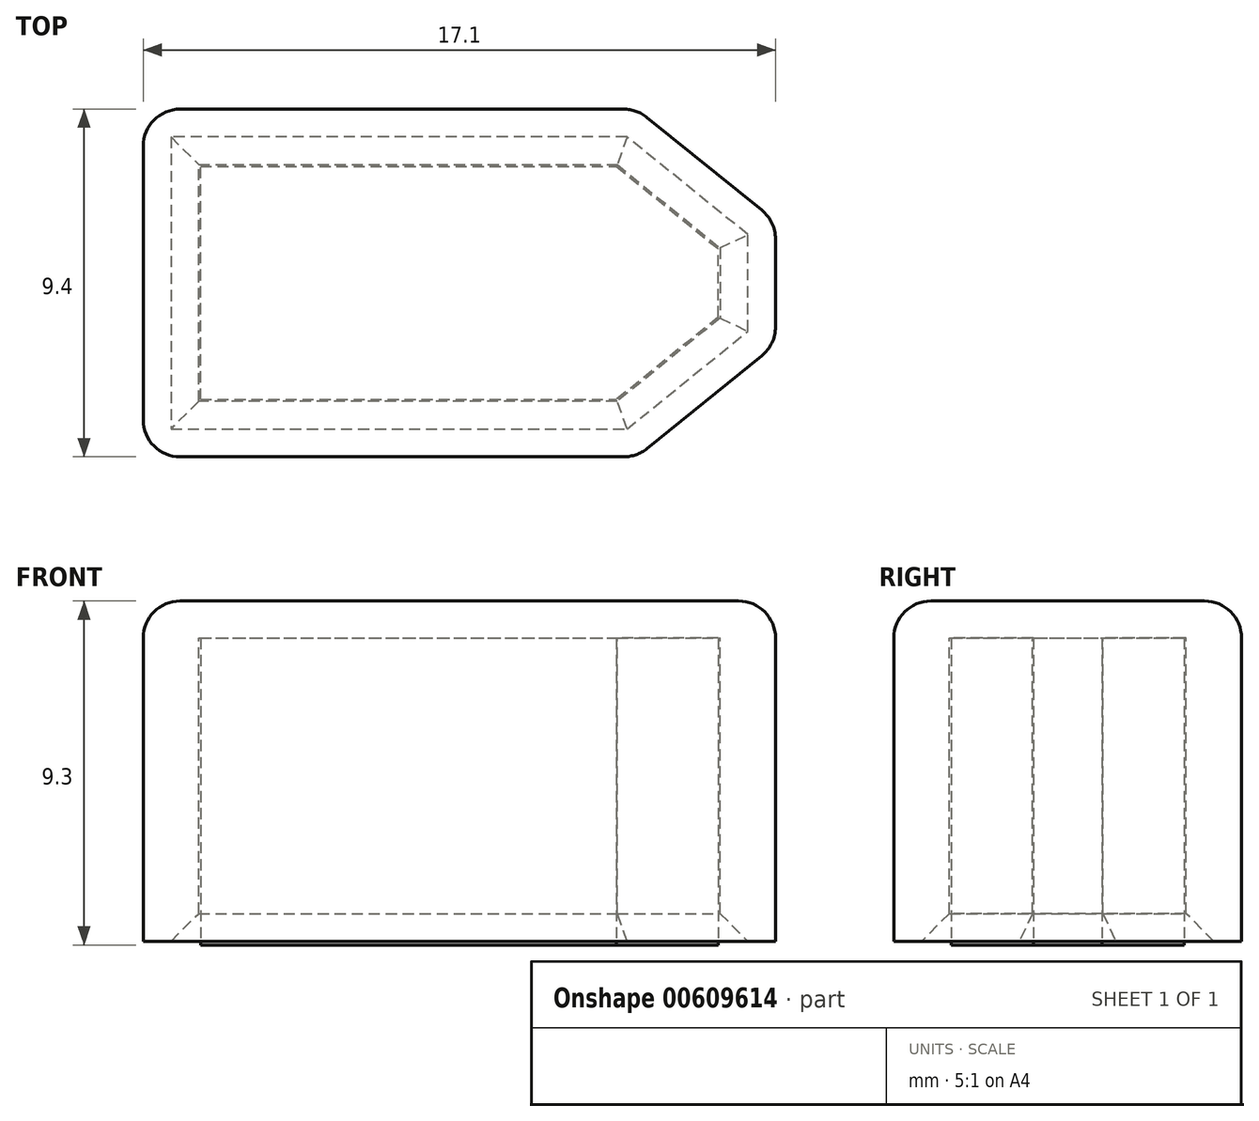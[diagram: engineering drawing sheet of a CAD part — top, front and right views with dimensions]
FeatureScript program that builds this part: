
annotation { "Feature Type Name" : "Feature", "Feature Type Description" : "" }
export const myFeature = defineFeature(function(context is Context, id is Id, definition is map)
    precondition{}
    {
        {
            var Q0;
            Q0=qCreatedBy(makeId("Top.planeOp"),FACE);
            var sketch = newSketch(context, id + "F0", { "sketchPlane" : qUnion([Q0])});
            skLineSegment(sketch, "E0.bottom", {"start": v(0, 0) * mm, "end": v(11.25, 0) * mm});
            skLineSegment(sketch, "E0.top", {"start": v(0, 6.3) * mm, "end": v(11.25, 6.3) * mm});
            skLineSegment(sketch, "E0.left", {"start": v(0, 0) * mm, "end": v(0, 6.3) * mm});
            skLineSegment(sketch, "E0.right", {"start": v(14, 2.22) * mm, "end": v(14, 4.08) * mm});
            skLineSegment(sketch, "E1", {"start": v(11.25, 6.3) * mm, "end": v(14, 4.08) * mm});
            skLineSegment(sketch, "E2", {"start": v(14, 2.22) * mm, "end": v(11.25, 0) * mm});
            skLineSegment(sketch, "E3", {"start": v(11.25, 6.3) * mm, "end": v(11.25, 0) * mm, "construction": true});
            skPoint(sketch, "E4.orphan", {"position": v(14, 0) * mm});
            skSolve(sketch);
        }
        {
            var Q0;
            Q0=makeQuery(id+"F0.imprint","IMPRINT",FACE,{"disambiguationData":[TD([[makeQuery(id+"F0.imprint","IMPRINT",EDGE,{"derivedFrom":sQuery(id+"F0.wireOp",EDGE,"E0.bottom")}),1.0]])]});
            extrude(context, id + "F1", {"entities" : qUnion([Q0]), "depth" : 8.3 * mm, "offsetDistance" : 25 * mm});
        }
        {
            var Q0;
            Q0=makeQuery(id+"F1.opExtrude","CAP_FACE",FACE,{"disambiguationData":[OSD([sQuery(id+"F0.wireOp",EDGE,"E0.bottom"),sQuery(id+"F0.wireOp",EDGE,"E0.top"),sQuery(id+"F0.wireOp",EDGE,"E0.left"),sQuery(id+"F0.wireOp",EDGE,"E0.right"),sQuery(id+"F0.wireOp",EDGE,"E1"),sQuery(id+"F0.wireOp",EDGE,"E2")])],"isStart":false});
            var sketch = newSketch(context, id + "F2", { "sketchPlane" : qUnion([Q0])});
            skLineSegment(sketch, "E5.0", {"start": v(-0.05, -0.05) * mm, "end": v(-0.05, 6.35) * mm});
            skLineSegment(sketch, "E5.1", {"start": v(11.27, 6.35) * mm, "end": v(14.05, 4.1) * mm});
            skLineSegment(sketch, "E5.2", {"start": v(14.05, 2.2) * mm, "end": v(14.05, 4.1) * mm});
            skLineSegment(sketch, "E5.3", {"start": v(-0.05, 6.35) * mm, "end": v(11.27, 6.35) * mm});
            skLineSegment(sketch, "E5.4", {"start": v(14.05, 2.2) * mm, "end": v(11.27, -0.05) * mm});
            skLineSegment(sketch, "E5.5", {"start": v(-0.05, -0.05) * mm, "end": v(11.27, -0.05) * mm});
            skLineSegment(sketch, "E6.0", {"start": v(-1.55, -1.55) * mm, "end": v(-1.55, 7.85) * mm});
            skLineSegment(sketch, "E6.1", {"start": v(11.8, 7.85) * mm, "end": v(15.55, 4.81) * mm});
            skLineSegment(sketch, "E6.2", {"start": v(15.55, 1.49) * mm, "end": v(15.55, 4.81) * mm});
            skLineSegment(sketch, "E6.3", {"start": v(-1.55, 7.85) * mm, "end": v(11.8, 7.85) * mm});
            skLineSegment(sketch, "E6.4", {"start": v(15.55, 1.49) * mm, "end": v(11.8, -1.55) * mm});
            skLineSegment(sketch, "E6.5", {"start": v(-1.55, -1.55) * mm, "end": v(11.8, -1.55) * mm});
            skSolve(sketch);
        }
        {
            var Q0;
            Q0=makeQuery(id+"F2.imprint","IMPRINT",FACE,{"disambiguationData":[TD([[makeQuery(id+"F2.imprint","IMPRINT",EDGE,{"derivedFrom":sQuery(id+"F2.wireOp",EDGE,"E5.0")}),1.0]])]});
            extrude(context, id + "F3", {"entities" : qUnion([Q0]), "oppositeDirection" : true, "depth" : 8.2 * mm, "offsetDistance" : 25 * mm});
        }
        {
            var Q0;
            Q0=makeQuery(id+"F3.opExtrude","CAP_FACE",FACE,{"disambiguationData":[OSD([sQuery(id+"F2.wireOp",EDGE,"E5.0"),sQuery(id+"F2.wireOp",EDGE,"E5.1"),sQuery(id+"F2.wireOp",EDGE,"E5.2"),sQuery(id+"F2.wireOp",EDGE,"E5.3"),sQuery(id+"F2.wireOp",EDGE,"E5.4"),sQuery(id+"F2.wireOp",EDGE,"E5.5"),sQuery(id+"F2.wireOp",EDGE,"E6.0"),sQuery(id+"F2.wireOp",EDGE,"E6.1"),sQuery(id+"F2.wireOp",EDGE,"E6.2"),sQuery(id+"F2.wireOp",EDGE,"E6.3"),sQuery(id+"F2.wireOp",EDGE,"E6.4"),sQuery(id+"F2.wireOp",EDGE,"E6.5")])],"isStart":true});
            var sketch = newSketch(context, id + "F4", { "sketchPlane" : qUnion([Q0])});
            skLineSegment(sketch, "E7", {"start": v(-1.55, 7.85) * mm, "end": v(-1.55, -1.55) * mm});
            skLineSegment(sketch, "E8", {"start": v(-1.55, -1.55) * mm, "end": v(11.8, -1.55) * mm});
            skLineSegment(sketch, "E9", {"start": v(11.8, -1.55) * mm, "end": v(15.55, 1.49) * mm});
            skLineSegment(sketch, "E10", {"start": v(15.55, 1.49) * mm, "end": v(15.55, 4.81) * mm});
            skLineSegment(sketch, "E11", {"start": v(15.55, 4.81) * mm, "end": v(11.8, 7.85) * mm});
            skLineSegment(sketch, "E12", {"start": v(11.8, 7.85) * mm, "end": v(-1.55, 7.85) * mm});
            skSolve(sketch);
        }
        {
            var Q0;
            Q0 = qSketchRegion(id + "F4", true);
            extrude(context, id + "F5", {"entities" : qUnion([Q0]), "operationType" : NewBodyOperationType.ADD, "depth" : 1 * mm, "offsetDistance" : 25 * mm});
        }
        {
            var Q0;
            Q0=makeQuery(id+"F5.opExtrude","CAP_FACE",FACE,{"disambiguationData":[OSD([sQuery(id+"F4.wireOp",EDGE,"E7"),sQuery(id+"F4.wireOp",EDGE,"E8"),sQuery(id+"F4.wireOp",EDGE,"E9"),sQuery(id+"F4.wireOp",EDGE,"E10"),sQuery(id+"F4.wireOp",EDGE,"E11"),sQuery(id+"F4.wireOp",EDGE,"E12")])],"isStart":false});
            var Q1;
            Q1=makeQuery(id+"F5.boolean.opBoolean","MERGE",EDGE,{"derivedFrom":[makeQuery(id+"F3.opExtrude","SWEPT_EDGE",EDGE,{"disambiguationData":[OSD([sQuery(id+"F2.wireOp",EDGE,"E6.0"),sQuery(id+"F2.wireOp",EDGE,"E6.5")])]}),makeQuery(id+"F5.opExtrude","SWEPT_EDGE",EDGE,{"disambiguationData":[OSD([sQuery(id+"F4.wireOp",EDGE,"E7"),sQuery(id+"F4.wireOp",EDGE,"E8")])]})]});
            var Q2;
            Q2=makeQuery(id+"F5.boolean.opBoolean","MERGE",EDGE,{"derivedFrom":[makeQuery(id+"F3.opExtrude","SWEPT_EDGE",EDGE,{"disambiguationData":[OSD([sQuery(id+"F2.wireOp",EDGE,"E6.0"),sQuery(id+"F2.wireOp",EDGE,"E6.3")])]}),makeQuery(id+"F5.opExtrude","SWEPT_EDGE",EDGE,{"disambiguationData":[OSD([sQuery(id+"F4.wireOp",EDGE,"E7"),sQuery(id+"F4.wireOp",EDGE,"E12")])]})]});
            var Q3;
            Q3=makeQuery(id+"F5.boolean.opBoolean","MERGE",EDGE,{"derivedFrom":[makeQuery(id+"F3.opExtrude","SWEPT_EDGE",EDGE,{"disambiguationData":[OSD([sQuery(id+"F2.wireOp",EDGE,"E6.1"),sQuery(id+"F2.wireOp",EDGE,"E6.3")])]}),makeQuery(id+"F5.opExtrude","SWEPT_EDGE",EDGE,{"disambiguationData":[OSD([sQuery(id+"F4.wireOp",EDGE,"E11"),sQuery(id+"F4.wireOp",EDGE,"E12")])]})]});
            var Q4;
            Q4=makeQuery(id+"F5.boolean.opBoolean","MERGE",EDGE,{"derivedFrom":[makeQuery(id+"F3.opExtrude","SWEPT_EDGE",EDGE,{"disambiguationData":[OSD([sQuery(id+"F2.wireOp",EDGE,"E6.1"),sQuery(id+"F2.wireOp",EDGE,"E6.2")])]}),makeQuery(id+"F5.opExtrude","SWEPT_EDGE",EDGE,{"disambiguationData":[OSD([sQuery(id+"F4.wireOp",EDGE,"E10"),sQuery(id+"F4.wireOp",EDGE,"E11")])]})]});
            var Q5;
            Q5=makeQuery(id+"F5.boolean.opBoolean","MERGE",EDGE,{"derivedFrom":[makeQuery(id+"F3.opExtrude","SWEPT_EDGE",EDGE,{"disambiguationData":[OSD([sQuery(id+"F2.wireOp",EDGE,"E6.2"),sQuery(id+"F2.wireOp",EDGE,"E6.4")])]}),makeQuery(id+"F5.opExtrude","SWEPT_EDGE",EDGE,{"disambiguationData":[OSD([sQuery(id+"F4.wireOp",EDGE,"E9"),sQuery(id+"F4.wireOp",EDGE,"E10")])]})]});
            var Q6;
            Q6=makeQuery(id+"F5.boolean.opBoolean","MERGE",EDGE,{"derivedFrom":[makeQuery(id+"F3.opExtrude","SWEPT_EDGE",EDGE,{"disambiguationData":[OSD([sQuery(id+"F2.wireOp",EDGE,"E6.4"),sQuery(id+"F2.wireOp",EDGE,"E6.5")])]}),makeQuery(id+"F5.opExtrude","SWEPT_EDGE",EDGE,{"disambiguationData":[OSD([sQuery(id+"F4.wireOp",EDGE,"E8"),sQuery(id+"F4.wireOp",EDGE,"E9")])]})]});
            fillet(context, id + "F6", {"entities" : qUnion([Q0, Q1, Q2, Q3, Q4, Q5, Q6]), "radius" : 1 * mm, "tangentPropagation" : true, "allowEdgeOverflow" : false});
        }
        {
            var Q0;
            Q0=makeQuery(id+"F3.opExtrude","CAP_EDGE",EDGE,{"disambiguationData":[OSD([sQuery(id+"F2.wireOp",EDGE,"E5.4")])],"isStart":false});
            var Q1;
            Q1=makeQuery(id+"F3.opExtrude","CAP_EDGE",EDGE,{"disambiguationData":[OSD([sQuery(id+"F2.wireOp",EDGE,"E5.2")])],"isStart":false});
            var Q2;
            Q2=makeQuery(id+"F3.opExtrude","CAP_EDGE",EDGE,{"disambiguationData":[OSD([sQuery(id+"F2.wireOp",EDGE,"E5.1")])],"isStart":false});
            var Q3;
            Q3=makeQuery(id+"F3.opExtrude","CAP_EDGE",EDGE,{"disambiguationData":[OSD([sQuery(id+"F2.wireOp",EDGE,"E5.3")])],"isStart":false});
            var Q4;
            Q4=makeQuery(id+"F3.opExtrude","CAP_EDGE",EDGE,{"disambiguationData":[OSD([sQuery(id+"F2.wireOp",EDGE,"E5.0")])],"isStart":false});
            var Q5;
            Q5=makeQuery(id+"F3.opExtrude","CAP_EDGE",EDGE,{"disambiguationData":[OSD([sQuery(id+"F2.wireOp",EDGE,"E5.5")])],"isStart":false});
            chamfer(context, id + "F7", {"entities" : qUnion([Q0, Q1, Q2, Q3, Q4, Q5]), "width" : .75 * mm, "tangentPropagation" : true});
        }
    });
